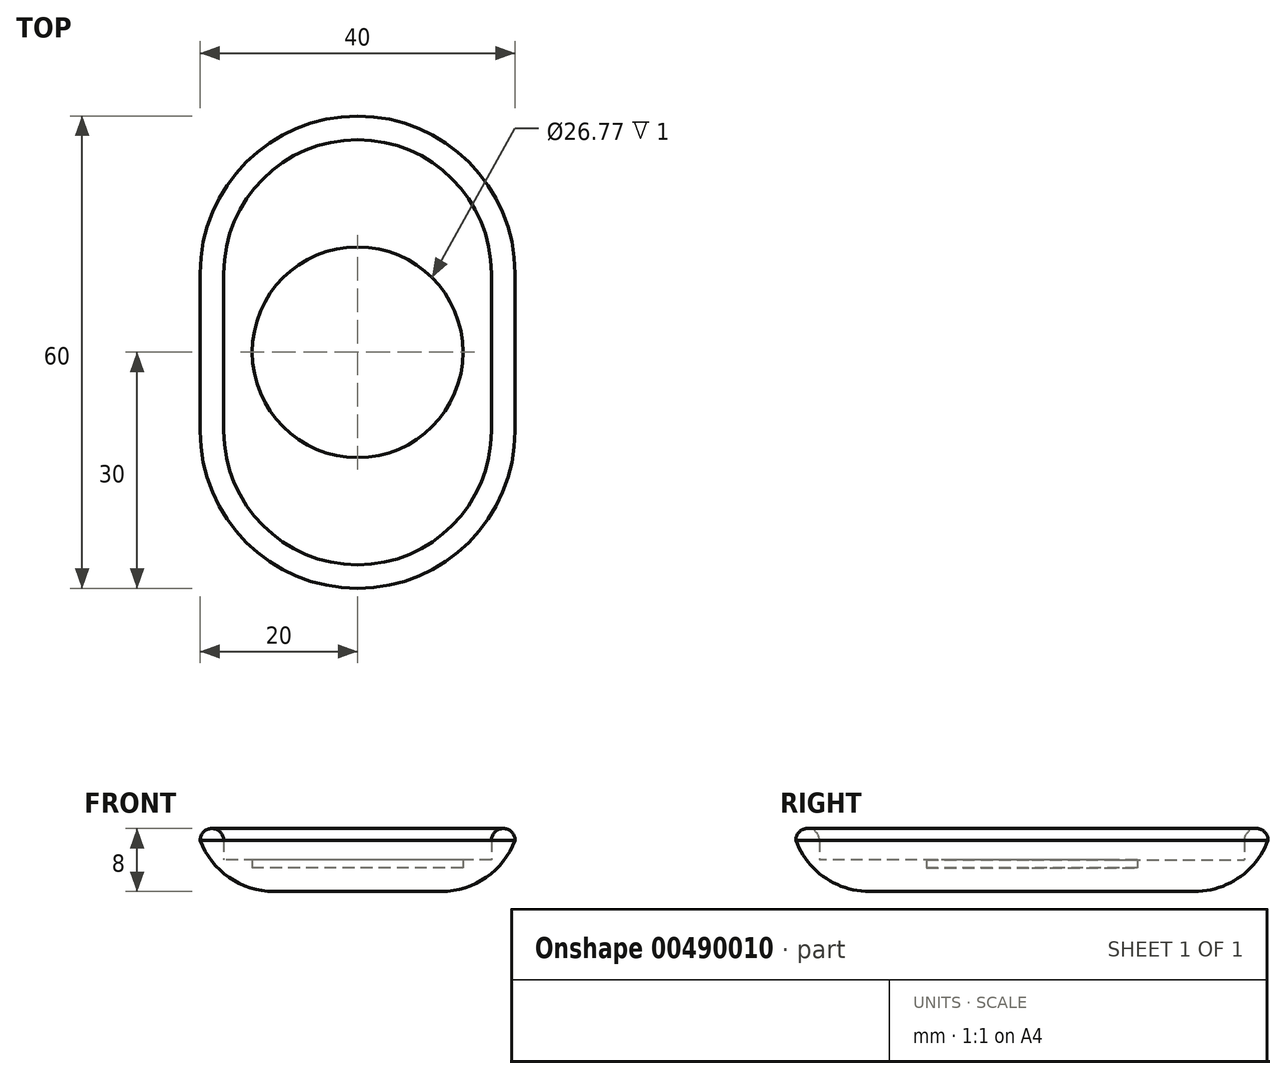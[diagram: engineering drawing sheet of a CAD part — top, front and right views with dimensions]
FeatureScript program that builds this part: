
annotation { "Feature Type Name" : "Feature", "Feature Type Description" : "" }
export const myFeature = defineFeature(function(context is Context, id is Id, definition is map)
    precondition{}
    {
        {
            var Q0;
            Q0=qCreatedBy(makeId("Top.planeOp"),FACE);
            var sketch = newSketch(context, id + "F0", { "sketchPlane" : qUnion([Q0])});
            skLineSegment(sketch, "E0.bottom", {"start": v(0, -30) * mm, "end": v(0, -30) * mm});
            skLineSegment(sketch, "E0.top", {"start": v(0, 30) * mm, "end": v(0, 30) * mm});
            skLineSegment(sketch, "E0.left", {"start": v(20, -10) * mm, "end": v(20, 10) * mm});
            skLineSegment(sketch, "E0.right", {"start": v(-20, -10) * mm, "end": v(-20, 10) * mm});
            skPoint(sketch, "E0.middle", {"position": v(0, 0) * mm});
            skPoint(sketch, "E1.visualSharp", {"position": v(-20, 30) * mm});
            skArc(sketch, "E1.filletArc", {"start": v(0, 30) * mm, "mid": v(-14.14, 24.14) * mm, "end": v(-20, 10) * mm});
            skPoint(sketch, "E2.visualSharp", {"position": v(20, 30) * mm});
            skArc(sketch, "E2.filletArc", {"start": v(20, 10) * mm, "mid": v(14.14, 24.14) * mm, "end": v(0, 30) * mm});
            skPoint(sketch, "E3.visualSharp", {"position": v(20, -30) * mm});
            skArc(sketch, "E3.filletArc", {"start": v(0, -30) * mm, "mid": v(14.14, -24.14) * mm, "end": v(20, -10) * mm});
            skPoint(sketch, "E4.visualSharp", {"position": v(-20, -30) * mm});
            skArc(sketch, "E4.filletArc", {"start": v(-20, -10) * mm, "mid": v(-14.14, -24.14) * mm, "end": v(0, -30) * mm});
            skLineSegment(sketch, "E5.0", {"start": v(17, -10) * mm, "end": v(17, 10) * mm});
            skArc(sketch, "E5.1", {"start": v(0, 27) * mm, "mid": v(-12.02, 22.02) * mm, "end": v(-17, 10) * mm});
            skLineSegment(sketch, "E5.2", {"start": v(-17, -10) * mm, "end": v(-17, 10) * mm});
            skArc(sketch, "E5.3", {"start": v(17, 10) * mm, "mid": v(12.02, 22.02) * mm, "end": v(0, 27) * mm});
            skArc(sketch, "E5.4", {"start": v(-17, -10) * mm, "mid": v(-12.02, -22.02) * mm, "end": v(0, -27) * mm});
            skArc(sketch, "E5.5", {"start": v(0, -27) * mm, "mid": v(12.02, -22.02) * mm, "end": v(17, -10) * mm});
            skCircle(sketch, "E6", {"center": v(0, 0) * mm, "radius": 13.39 * mm});
            skSolve(sketch);
        }
        {
            var Q0;
            Q0=makeQuery(id+"F0.imprint","IMPRINT",FACE,{"disambiguationData":[TD([[makeQuery(id+"F0.imprint","IMPRINT",EDGE,{"derivedFrom":sQuery(id+"F0.wireOp",EDGE,"E0.left")}),1.0]])]});
            var Q1;
            Q1=makeQuery(id+"F0.imprint","IMPRINT",FACE,{"disambiguationData":[TD([[makeQuery(id+"F0.imprint","IMPRINT",EDGE,{"derivedFrom":sQuery(id+"F0.wireOp",EDGE,"E5.0")}),1.0]])]});
            extrude(context, id + "F1", {"entities" : qUnion([Q0, Q1]), "depth" : 4 * mm});
        }
        {
            var Q0;
            Q0=makeQuery(id+"F0.imprint","IMPRINT",FACE,{"disambiguationData":[TD([[makeQuery(id+"F0.imprint","IMPRINT",EDGE,{"derivedFrom":sQuery(id+"F0.wireOp",EDGE,"E0.left")}),1.0]])]});
            extrude(context, id + "F2", {"entities" : qUnion([Q0]), "operationType" : NewBodyOperationType.ADD, "depth" : 8 * mm});
        }
        {
            var Q0;
            Q0=makeQuery(id+"F0.imprint","IMPRINT",FACE,{"disambiguationData":[TD([[makeQuery(id+"F0.imprint","IMPRINT",EDGE,{"derivedFrom":sQuery(id+"F0.wireOp",EDGE,"E6")}),1.0]])]});
            extrude(context, id + "F3", {"entities" : qUnion([Q0]), "operationType" : NewBodyOperationType.ADD, "depth" : 3 * mm});
        }
        {
            var Q0;
            Q0=makeQuery(id+"F2.opExtrude","CAP_EDGE",EDGE,{"disambiguationData":[OSD([sQuery(id+"F0.wireOp",EDGE,"E5.0")])],"isStart":false});
            var Q1;
            Q1=makeQuery(id+"F2.opExtrude","CAP_EDGE",EDGE,{"disambiguationData":[OSD([sQuery(id+"F0.wireOp",EDGE,"E5.4"),sQuery(id+"F0.wireOp",EDGE,"E5.5")])],"isStart":false});
            var Q2;
            Q2=makeQuery(id+"F2.opExtrude","CAP_EDGE",EDGE,{"disambiguationData":[OSD([sQuery(id+"F0.wireOp",EDGE,"E5.1"),sQuery(id+"F0.wireOp",EDGE,"E5.3")])],"isStart":false});
            var Q3;
            Q3=makeQuery(id+"F2.opExtrude","CAP_EDGE",EDGE,{"disambiguationData":[OSD([sQuery(id+"F0.wireOp",EDGE,"E0.left")])],"isStart":false});
            fillet(context, id + "F4", {"entities" : qUnion([Q0, Q1, Q2, Q3]), "radius" : 1.5 * mm, "tangentPropagation" : true, "allowEdgeOverflow" : false});
        }
        {
            var Q0;
            Q0=makeQuery(id+"F1.opExtrude","CAP_EDGE",EDGE,{"disambiguationData":[OSD([sQuery(id+"F0.wireOp",EDGE,"E3.filletArc"),sQuery(id+"F0.wireOp",EDGE,"E4.filletArc")])],"isStart":true});
            var Q1;
            Q1=makeQuery(id+"F1.opExtrude","CAP_EDGE",EDGE,{"disambiguationData":[OSD([sQuery(id+"F0.wireOp",EDGE,"E0.right")])],"isStart":true});
            fillet(context, id + "F5", {"entities" : qUnion([Q0, Q1]), "radius" : 10 * mm, "tangentPropagation" : true, "allowEdgeOverflow" : false});
        }
    });
